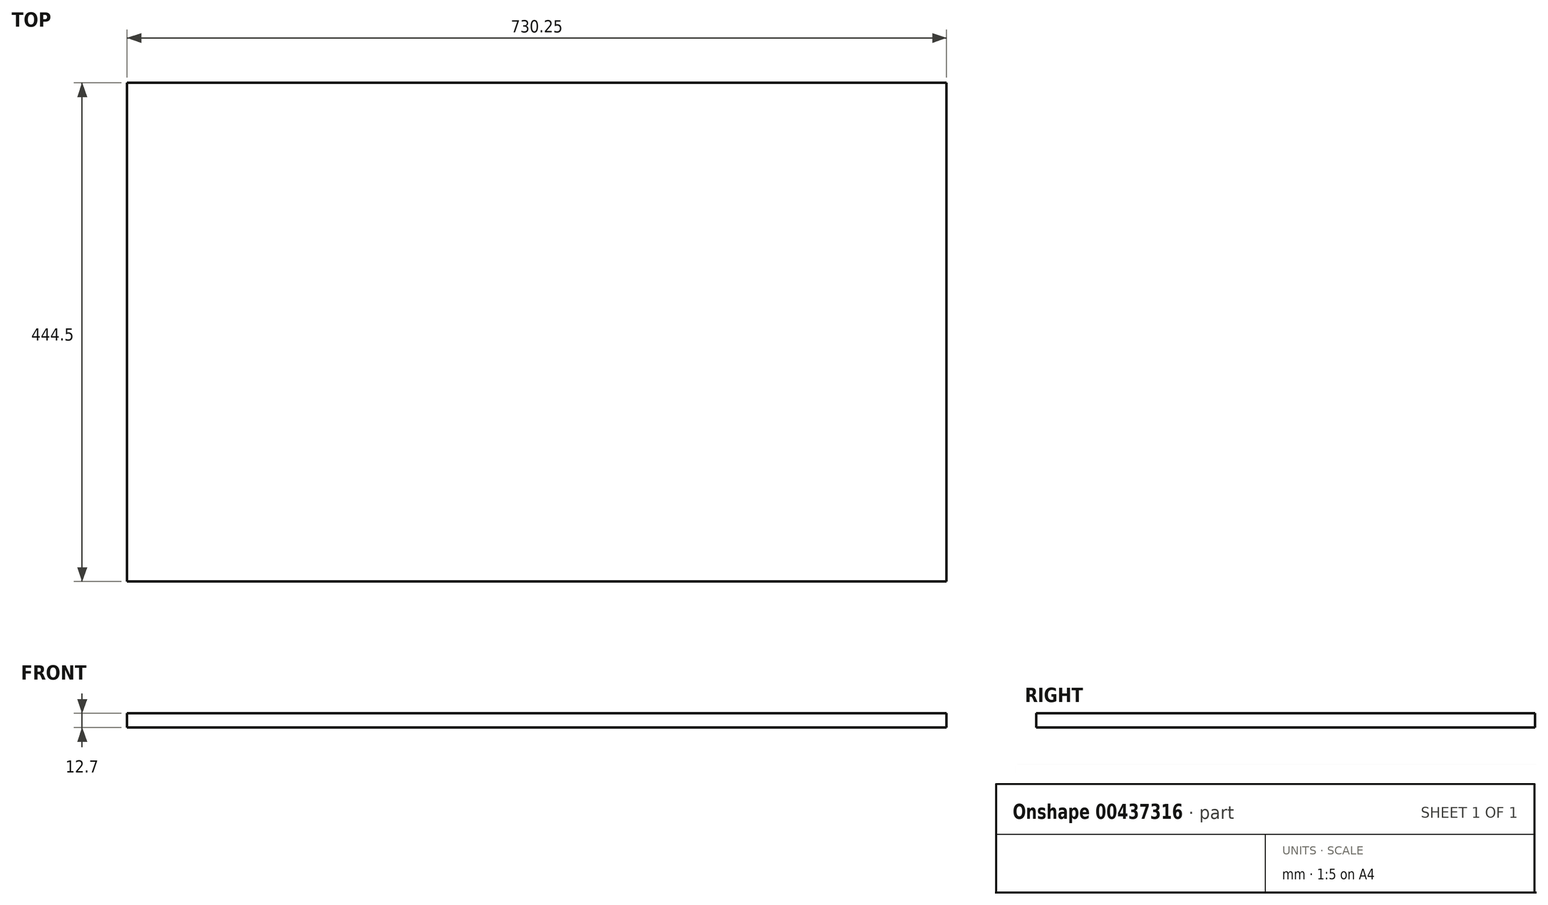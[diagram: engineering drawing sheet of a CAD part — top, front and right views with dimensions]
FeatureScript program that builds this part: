
annotation { "Feature Type Name" : "Feature", "Feature Type Description" : "" }
export const myFeature = defineFeature(function(context is Context, id is Id, definition is map)
    precondition{}
    {
        {
            var Q0;
            Q0=qCreatedBy(makeId("Top.planeOp"),FACE);
            var sketch = newSketch(context, id + "F0", { "sketchPlane" : qUnion([Q0])});
            skLineSegment(sketch, "E0.bottom", {"start": v(0, 0) * mm, "end": v(730.25, 0) * mm});
            skLineSegment(sketch, "E0.top", {"start": v(0, 444.5) * mm, "end": v(730.25, 444.5) * mm});
            skLineSegment(sketch, "E0.left", {"start": v(0, 0) * mm, "end": v(0, 444.5) * mm});
            skLineSegment(sketch, "E0.right", {"start": v(730.25, 0) * mm, "end": v(730.25, 444.5) * mm});
            skSolve(sketch);
        }
        {
            var Q0;
            Q0=makeQuery(id+"F0.imprint","IMPRINT",FACE,{"disambiguationData":[TD([[makeQuery(id+"F0.imprint","IMPRINT",EDGE,{"derivedFrom":sQuery(id+"F0.wireOp",EDGE,"E0.bottom")}),1.0]])]});
            extrude(context, id + "F1", {"entities" : qUnion([Q0]), "depth" : 12.7 * mm});
        }
    });
